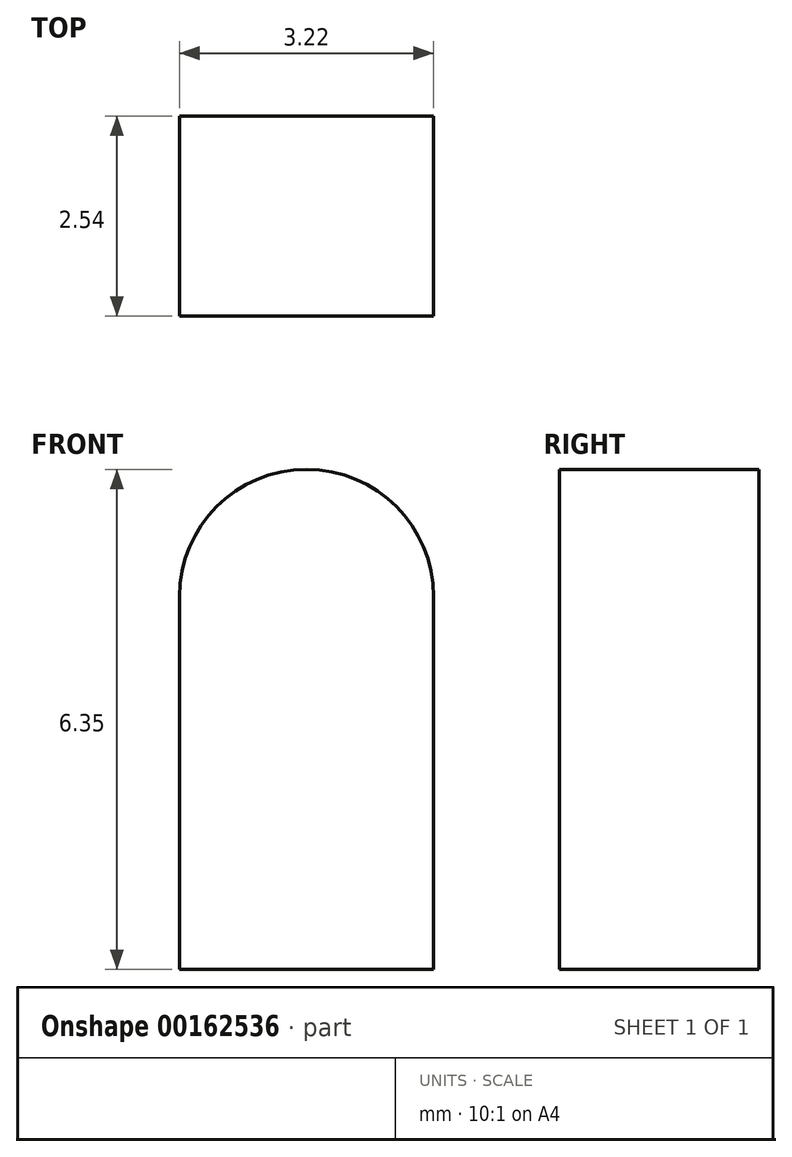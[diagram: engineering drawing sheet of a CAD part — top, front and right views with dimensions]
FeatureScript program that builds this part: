
annotation { "Feature Type Name" : "Feature", "Feature Type Description" : "" }
export const myFeature = defineFeature(function(context is Context, id is Id, definition is map)
    precondition{}
    {
        {
            var Q0;
            Q0=qCreatedBy(makeId("Front.planeOp"),FACE);
            var sketch = newSketch(context, id + "F0", { "sketchPlane" : qUnion([Q0])});
            skLineSegment(sketch, "E0.bottom", {"start": v(1.61, 2.37) * mm, "end": v(-1.61, 2.37) * mm});
            skLineSegment(sketch, "E0.top", {"start": v(1.61, -2.37) * mm, "end": v(-1.61, -2.37) * mm});
            skLineSegment(sketch, "E0.left", {"start": v(1.61, 2.37) * mm, "end": v(1.61, -2.37) * mm});
            skLineSegment(sketch, "E0.right", {"start": v(-1.61, 2.37) * mm, "end": v(-1.61, -2.37) * mm});
            skPoint(sketch, "E0.middle", {"position": v(0, 0) * mm});
            skArc(sketch, "E1", {"start": v(1.61, 2.37) * mm, "mid": v(0, 3.98) * mm, "end": v(-1.61, 2.37) * mm});
            skSolve(sketch);
        }
        {
            var Q0;
            Q0 = qSketchRegion(id + "F0", true);
            extrude(context, id + "F1", {"entities" : qUnion([Q0]), "depth" : 2.54 * mm});
        }
    });
